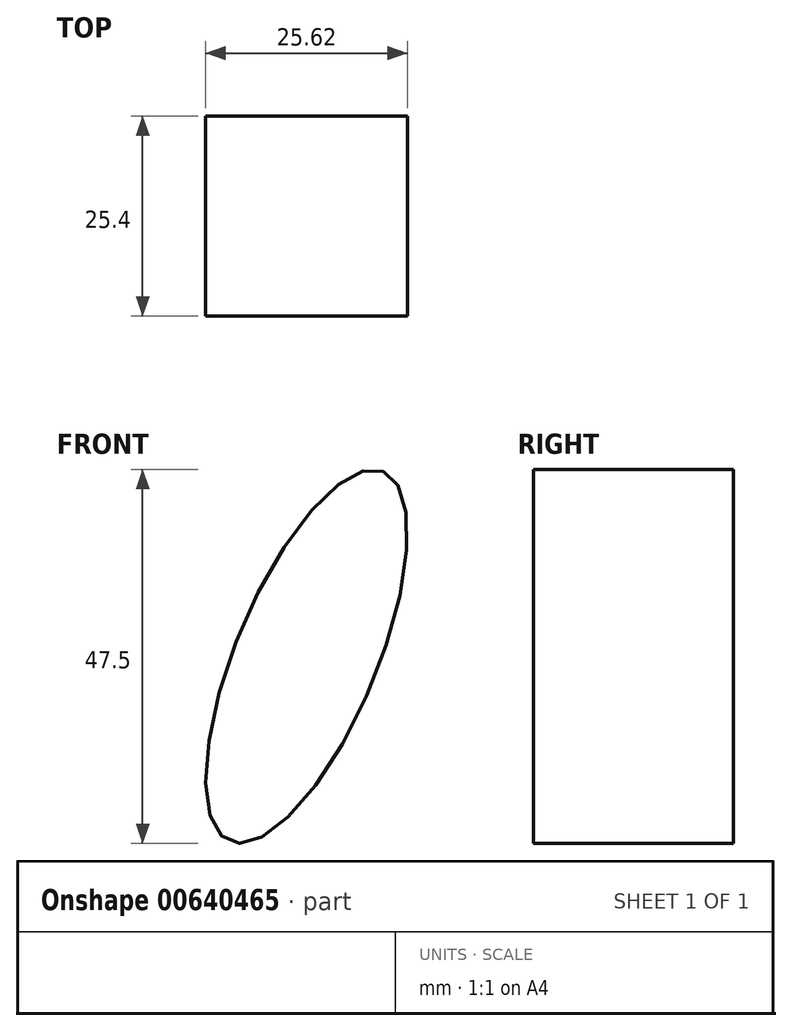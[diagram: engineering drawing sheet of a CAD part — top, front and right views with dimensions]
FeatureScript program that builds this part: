
annotation { "Feature Type Name" : "Feature", "Feature Type Description" : "" }
export const myFeature = defineFeature(function(context is Context, id is Id, definition is map)
    precondition{}
    {
        {
            var Q0;
            Q0=qCreatedBy(makeId("Front.planeOp"),FACE);
            var sketch = newSketch(context, id + "F0", { "sketchPlane" : qUnion([Q0])});
            skEllipse(sketch, "E0", {"center": v(0, 0) * mm, "majorRadius": 25.45 * mm, "minorRadius": 8.98 * mm, "majorAxis": v(0.38, 0.92)});
            skSolve(sketch);
        }
        {
            var Q0;
            Q0=makeQuery(id+"F0.imprint","IMPRINT",FACE,{"disambiguationData":[TD([[makeQuery(id+"F0.imprint","IMPRINT",EDGE,{"derivedFrom":sQuery(id+"F0.wireOp",EDGE,"E0")}),1.0]])]});
            extrude(context, id + "F1", {"entities" : qUnion([Q0]), "depth" : 25.4 * mm, "offsetDistance" : 25.4 * mm});
        }
    });
